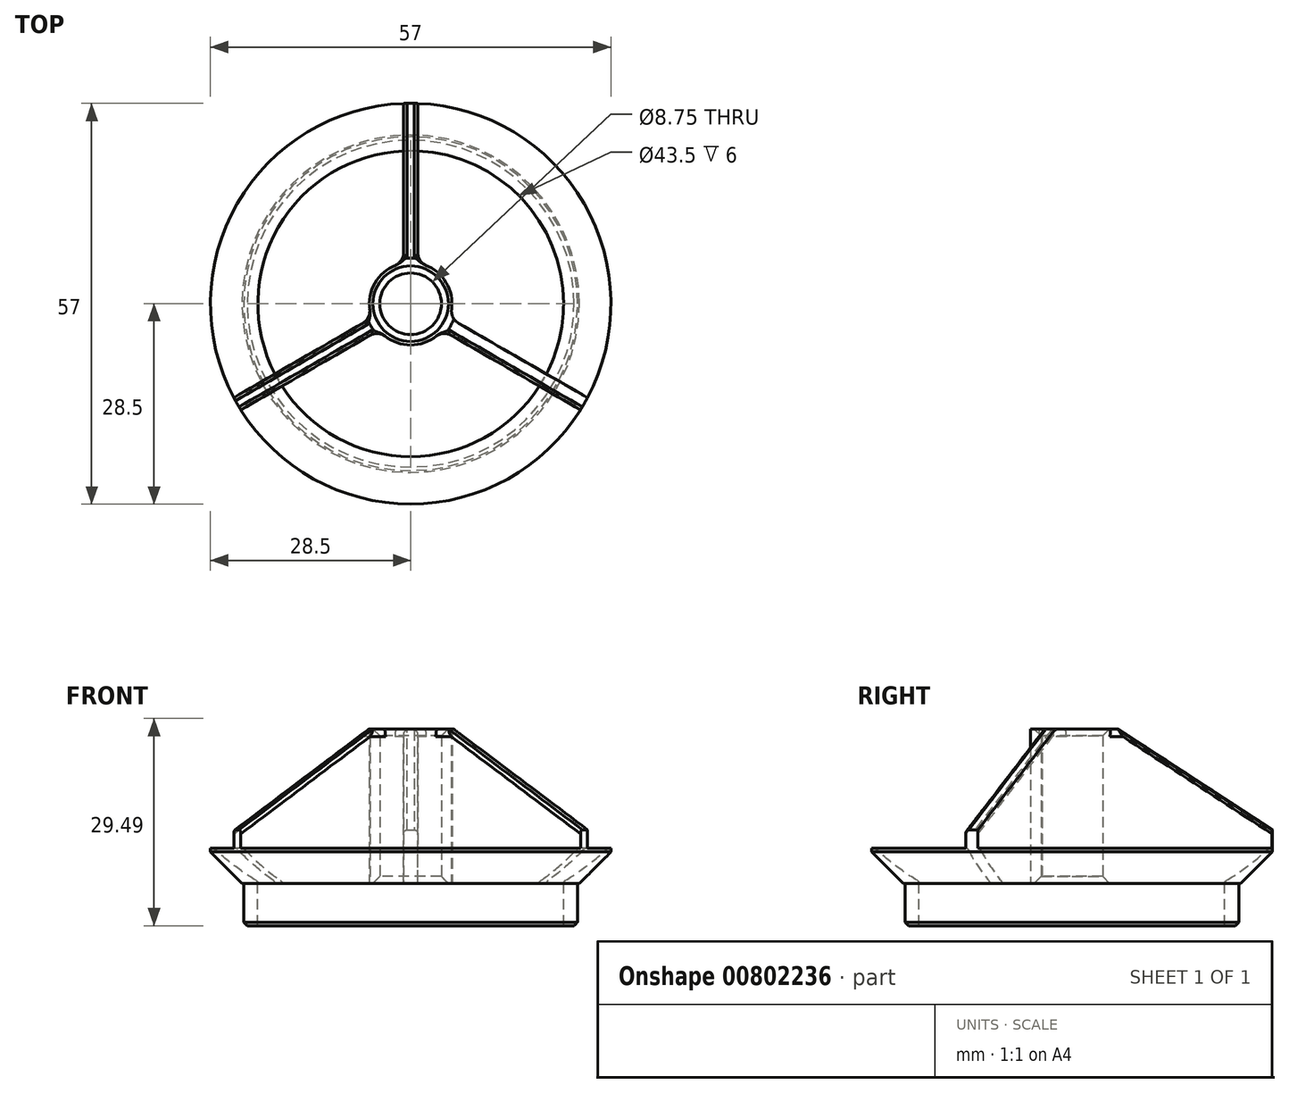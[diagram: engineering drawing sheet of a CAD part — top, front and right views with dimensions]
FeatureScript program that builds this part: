
annotation { "Feature Type Name" : "Feature", "Feature Type Description" : "" }
export const myFeature = defineFeature(function(context is Context, id is Id, definition is map)
    precondition{}
    {
        {
            var Q0;
            Q0=qCreatedBy(makeId("Top.planeOp"),FACE);
            var sketch = newSketch(context, id + "F0", { "sketchPlane" : qUnion([Q0])});
            skCircle(sketch, "E0", {"center": v(0, 0) * mm, "radius": 29.5 * mm});
            skCircle(sketch, "E1", {"center": v(0, 0) * mm, "radius": 4.38 * mm});
            skCircle(sketch, "E2", {"center": v(0, 0) * mm, "radius": 5.88 * mm});
            skCircle(sketch, "E3", {"center": v(0, 0) * mm, "radius": 22.5 * mm});
            skLineSegment(sketch, "E4", {"start": v(-1, 22.48) * mm, "end": v(-1, 5.79) * mm});
            skLineSegment(sketch, "E5", {"start": v(1, 5.79) * mm, "end": v(1, 22.48) * mm});
            skLineSegment(sketch, "E6", {"start": v(-1, 22.48) * mm, "end": v(-1, 29.48) * mm});
            skLineSegment(sketch, "E7", {"start": v(1, 22.48) * mm, "end": v(1, 29.48) * mm});
            skCircle(sketch, "E8", {"center": v(0, 0) * mm, "radius": 28.5 * mm});
            skLineSegment(sketch, "E9.1.0", {"start": v(-19.97, -10.37) * mm, "end": v(-26.03, -13.88) * mm});
            skLineSegment(sketch, "E9.1.1", {"start": v(-18.97, -12.1) * mm, "end": v(-25.03, -15.6) * mm});
            skLineSegment(sketch, "E9.1.2", {"start": v(-18.97, -12.1) * mm, "end": v(-4.51, -3.76) * mm});
            skLineSegment(sketch, "E9.1.3", {"start": v(-5.51, -2.03) * mm, "end": v(-19.97, -10.37) * mm});
            skLineSegment(sketch, "E9.2.0", {"start": v(18.97, -12.1) * mm, "end": v(25.03, -15.6) * mm});
            skLineSegment(sketch, "E9.2.1", {"start": v(19.97, -10.37) * mm, "end": v(26.03, -13.88) * mm});
            skLineSegment(sketch, "E9.2.2", {"start": v(19.97, -10.37) * mm, "end": v(5.51, -2.03) * mm});
            skLineSegment(sketch, "E9.2.3", {"start": v(4.51, -3.76) * mm, "end": v(18.97, -12.1) * mm});
            skSolve(sketch);
        }
        {
            var Q0;
            {var subQ0=sQuery(id+"F0.wireOp",EDGE,"E6");var subQ5=sQuery(id+"F0.wireOp",EDGE,"E8");var subQ6=makeQuery(id+"F0.imprint","INTERSECT",VERTEX,{"derivedFrom":[subQ0,subQ5]});Q0=makeQuery(id+"F0.imprint","IMPRINT",FACE,{"disambiguationData":[TD([[makeQuery(id+"F0.imprint","IMPRINT",EDGE,{"disambiguationData":[TD([[subQ6,-1.0]])],"derivedFrom":subQ5}),1.0]])]});}
            var Q1;
            {var subQ0=sQuery(id+"F0.wireOp",EDGE,"E7");var subQ5=sQuery(id+"F0.wireOp",EDGE,"E8");var subQ7=makeQuery(id+"F0.imprint","INTERSECT",VERTEX,{"derivedFrom":[subQ0,subQ5]});Q1=makeQuery(id+"F0.imprint","IMPRINT",FACE,{"disambiguationData":[TD([[makeQuery(id+"F0.imprint","IMPRINT",EDGE,{"disambiguationData":[TD([[subQ7,1.0]])],"derivedFrom":subQ5}),1.0]])]});}
            var Q2;
            {var subQ0=sQuery(id+"F0.wireOp",EDGE,"6sBZeKKk-kEEp-gHMs-JJ9J-U2pvovovTZg0");var subQ5=sQuery(id+"F0.wireOp",EDGE,"E8");var subQ7=makeQuery(id+"F0.imprint","INTERSECT",VERTEX,{"derivedFrom":[subQ0,subQ5]});Q2=makeQuery(id+"F0.imprint","IMPRINT",FACE,{"disambiguationData":[TD([[makeQuery(id+"F0.imprint","IMPRINT",EDGE,{"disambiguationData":[TD([[subQ7,1.0]])],"derivedFrom":subQ5}),1.0]])]});}
            var Q3;
            {var subQ0=sQuery(id+"F0.wireOp",EDGE,"7a49S09U-4TKs-Mau8-UFGr-jYDSAMmVkobc");var subQ5=sQuery(id+"F0.wireOp",EDGE,"E8");var subQ6=makeQuery(id+"F0.imprint","INTERSECT",VERTEX,{"derivedFrom":[subQ0,subQ5]});Q3=makeQuery(id+"F0.imprint","IMPRINT",FACE,{"disambiguationData":[TD([[makeQuery(id+"F0.imprint","IMPRINT",EDGE,{"disambiguationData":[TD([[subQ6,1.0]])],"derivedFrom":subQ5}),1.0]])]});}
            var Q4;
            {var subQ0=sQuery(id+"F0.wireOp",EDGE,"7a49S09U-4TKs-Mau8-UFGr-jYDSAMmVkobc");var subQ1=sQuery(id+"F0.wireOp",EDGE,"E0");var subQ2=makeQuery(id+"F0.imprint","INTERSECT",VERTEX,{"derivedFrom":[subQ1,subQ0]});Q4=makeQuery(id+"F0.imprint","IMPRINT",FACE,{"disambiguationData":[TD([[makeQuery(id+"F0.imprint","IMPRINT",EDGE,{"disambiguationData":[TD([[subQ2,1.0]])],"derivedFrom":subQ1}),1.0]])]});}
            var Q5;
            {var subQ0=sQuery(id+"F0.wireOp",EDGE,"E6");var subQ1=sQuery(id+"F0.wireOp",EDGE,"E0");var subQ2=makeQuery(id+"F0.imprint","INTERSECT",VERTEX,{"derivedFrom":[subQ1,subQ0]});Q5=makeQuery(id+"F0.imprint","IMPRINT",FACE,{"disambiguationData":[TD([[makeQuery(id+"F0.imprint","IMPRINT",EDGE,{"disambiguationData":[TD([[subQ2,-1.0]])],"derivedFrom":subQ1}),1.0]])]});}
            var Q6;
            {var subQ0=sQuery(id+"F0.wireOp",EDGE,"E7");var subQ1=sQuery(id+"F0.wireOp",EDGE,"E0");var subQ2=makeQuery(id+"F0.imprint","INTERSECT",VERTEX,{"derivedFrom":[subQ1,subQ0]});Q6=makeQuery(id+"F0.imprint","IMPRINT",FACE,{"disambiguationData":[TD([[makeQuery(id+"F0.imprint","IMPRINT",EDGE,{"disambiguationData":[TD([[subQ2,1.0]])],"derivedFrom":subQ1}),1.0]])]});}
            var Q7;
            {var subQ0=sQuery(id+"F0.wireOp",EDGE,"6sBZeKKk-kEEp-gHMs-JJ9J-U2pvovovTZg0");var subQ1=sQuery(id+"F0.wireOp",EDGE,"E0");var subQ2=makeQuery(id+"F0.imprint","INTERSECT",VERTEX,{"derivedFrom":[subQ1,subQ0]});Q7=makeQuery(id+"F0.imprint","IMPRINT",FACE,{"disambiguationData":[TD([[makeQuery(id+"F0.imprint","IMPRINT",EDGE,{"disambiguationData":[TD([[subQ2,1.0]])],"derivedFrom":subQ1}),1.0]])]});}
            var Q8;
            {var subQ0=sQuery(id+"F0.wireOp",EDGE,"kpPb6oPH-wYUV-R5u9-Nvo8-y8tA6iOcowlW");var subQ5=sQuery(id+"F0.wireOp",EDGE,"E8");var subQ7=makeQuery(id+"F0.imprint","INTERSECT",VERTEX,{"derivedFrom":[subQ0,subQ5]});Q8=makeQuery(id+"F0.imprint","IMPRINT",FACE,{"disambiguationData":[TD([[makeQuery(id+"F0.imprint","IMPRINT",EDGE,{"disambiguationData":[TD([[subQ7,1.0]])],"derivedFrom":subQ5}),1.0]])]});}
            var Q9;
            {var subQ0=sQuery(id+"F0.wireOp",EDGE,"kpPb6oPH-wYUV-R5u9-Nvo8-y8tA6iOcowlW");var subQ1=sQuery(id+"F0.wireOp",EDGE,"E0");var subQ2=makeQuery(id+"F0.imprint","INTERSECT",VERTEX,{"derivedFrom":[subQ1,subQ0]});Q9=makeQuery(id+"F0.imprint","IMPRINT",FACE,{"disambiguationData":[TD([[makeQuery(id+"F0.imprint","IMPRINT",EDGE,{"disambiguationData":[TD([[subQ2,1.0]])],"derivedFrom":subQ1}),1.0]])]});}
            var Q10;
            {var subQ0=sQuery(id+"F0.wireOp",EDGE,"64FUqdOZ-ZsVY-jkXw-3n9p-KAZBQBVsTFE5");var subQ1=sQuery(id+"F0.wireOp",EDGE,"E0");var subQ2=makeQuery(id+"F0.imprint","INTERSECT",VERTEX,{"derivedFrom":[subQ1,subQ0]});Q10=makeQuery(id+"F0.imprint","IMPRINT",FACE,{"disambiguationData":[TD([[makeQuery(id+"F0.imprint","IMPRINT",EDGE,{"disambiguationData":[TD([[subQ2,-1.0]])],"derivedFrom":subQ1}),1.0]])]});}
            var Q11;
            {var subQ0=sQuery(id+"F0.wireOp",EDGE,"64FUqdOZ-ZsVY-jkXw-3n9p-KAZBQBVsTFE5");var subQ5=sQuery(id+"F0.wireOp",EDGE,"E8");var subQ6=makeQuery(id+"F0.imprint","INTERSECT",VERTEX,{"derivedFrom":[subQ0,subQ5]});Q11=makeQuery(id+"F0.imprint","IMPRINT",FACE,{"disambiguationData":[TD([[makeQuery(id+"F0.imprint","IMPRINT",EDGE,{"disambiguationData":[TD([[subQ6,-1.0]])],"derivedFrom":subQ5}),1.0]])]});}
            var Q12;
            {var subQ0=sQuery(id+"F0.wireOp",EDGE,"E6");var subQ5=sQuery(id+"F0.wireOp",EDGE,"E8");var subQ6=makeQuery(id+"F0.imprint","INTERSECT",VERTEX,{"derivedFrom":[subQ0,subQ5]});Q12=makeQuery(id+"F0.imprint","IMPRINT",FACE,{"disambiguationData":[TD([[makeQuery(id+"F0.imprint","IMPRINT",EDGE,{"disambiguationData":[TD([[subQ6,1.0]])],"derivedFrom":subQ5}),1.0]])]});}
            var Q13;
            {var subQ0=sQuery(id+"F0.wireOp",EDGE,"E6");var subQ1=sQuery(id+"F0.wireOp",EDGE,"E0");var subQ2=makeQuery(id+"F0.imprint","INTERSECT",VERTEX,{"derivedFrom":[subQ1,subQ0]});Q13=makeQuery(id+"F0.imprint","IMPRINT",FACE,{"disambiguationData":[TD([[makeQuery(id+"F0.imprint","IMPRINT",EDGE,{"disambiguationData":[TD([[subQ2,1.0]])],"derivedFrom":subQ1}),1.0]])]});}
            var Q14;
            {var subQ0=sQuery(id+"F0.wireOp",EDGE,"7a49S09U-4TKs-Mau8-UFGr-jYDSAMmVkobc");var subQ5=sQuery(id+"F0.wireOp",EDGE,"E8");var subQ6=makeQuery(id+"F0.imprint","INTERSECT",VERTEX,{"derivedFrom":[subQ0,subQ5]});Q14=makeQuery(id+"F0.imprint","IMPRINT",FACE,{"disambiguationData":[TD([[makeQuery(id+"F0.imprint","IMPRINT",EDGE,{"disambiguationData":[TD([[subQ6,-1.0]])],"derivedFrom":subQ5}),1.0]])]});}
            var Q15;
            {var subQ0=sQuery(id+"F0.wireOp",EDGE,"7a49S09U-4TKs-Mau8-UFGr-jYDSAMmVkobc");var subQ1=sQuery(id+"F0.wireOp",EDGE,"E0");var subQ2=makeQuery(id+"F0.imprint","INTERSECT",VERTEX,{"derivedFrom":[subQ1,subQ0]});Q15=makeQuery(id+"F0.imprint","IMPRINT",FACE,{"disambiguationData":[TD([[makeQuery(id+"F0.imprint","IMPRINT",EDGE,{"disambiguationData":[TD([[subQ2,-1.0]])],"derivedFrom":subQ1}),1.0]])]});}
            extrude(context, id + "F1", {"entities" : qUnion([Q0, Q1, Q2, Q3, Q4, Q5, Q6, Q7, Q8, Q9, Q10, Q11, Q12, Q13, Q14, Q15]), "depth" : 5 * mm, "offsetDistance" : 25 * mm});
        }
        {
            var Q0;
            {var subQ0=sQuery(id+"F0.wireOp",EDGE,"E9.2.2");Q0=makeQuery(id+"F0.imprint","IMPRINT",FACE,{"disambiguationData":[TD([[makeQuery(id+"F0.imprint","IMPRINT",EDGE,{"derivedFrom":subQ0}),1.0]])]});}
            var Q1;
            Q1=makeQuery(id+"F0.imprint","IMPRINT",FACE,{"disambiguationData":[TD([[makeQuery(id+"F0.imprint","IMPRINT",EDGE,{"derivedFrom":sQuery(id+"F0.wireOp",EDGE,"E1")}),-1.0]])]});
            var Q2;
            {var subQ0=sQuery(id+"F0.wireOp",EDGE,"E9.1.2");Q2=makeQuery(id+"F0.imprint","IMPRINT",FACE,{"disambiguationData":[TD([[makeQuery(id+"F0.imprint","IMPRINT",EDGE,{"derivedFrom":subQ0}),1.0]])]});}
            var Q3;
            {var subQ0=sQuery(id+"F0.wireOp",EDGE,"E4");Q3=makeQuery(id+"F0.imprint","IMPRINT",FACE,{"disambiguationData":[TD([[makeQuery(id+"F0.imprint","IMPRINT",EDGE,{"derivedFrom":subQ0}),1.0]])]});}
            var Q4;
            {var subQ0=sQuery(id+"F0.wireOp",EDGE,"E9.1.0");var subQ5=sQuery(id+"F0.wireOp",EDGE,"E8");var subQ6=makeQuery(id+"F0.imprint","INTERSECT",VERTEX,{"derivedFrom":[subQ5,subQ0]});Q4=makeQuery(id+"F0.imprint","IMPRINT",FACE,{"disambiguationData":[TD([[makeQuery(id+"F0.imprint","IMPRINT",EDGE,{"disambiguationData":[TD([[subQ6,-1.0]])],"derivedFrom":subQ5}),1.0]])]});}
            var Q5;
            {var subQ0=sQuery(id+"F0.wireOp",EDGE,"E9.2.0");var subQ5=sQuery(id+"F0.wireOp",EDGE,"E8");var subQ6=makeQuery(id+"F0.imprint","INTERSECT",VERTEX,{"derivedFrom":[subQ5,subQ0]});Q5=makeQuery(id+"F0.imprint","IMPRINT",FACE,{"disambiguationData":[TD([[makeQuery(id+"F0.imprint","IMPRINT",EDGE,{"disambiguationData":[TD([[subQ6,-1.0]])],"derivedFrom":subQ5}),1.0]])]});}
            var Q6;
            {var subQ0=sQuery(id+"F0.wireOp",EDGE,"E6");var subQ5=sQuery(id+"F0.wireOp",EDGE,"E8");var subQ7=makeQuery(id+"F0.imprint","INTERSECT",VERTEX,{"derivedFrom":[subQ0,subQ5]});Q6=makeQuery(id+"F0.imprint","IMPRINT",FACE,{"disambiguationData":[TD([[makeQuery(id+"F0.imprint","IMPRINT",EDGE,{"disambiguationData":[TD([[subQ7,1.0]])],"derivedFrom":subQ5}),1.0]])]});}
            var Q7;
            {var subQ0=sQuery(id+"F0.wireOp",EDGE,"E9.2.0");var subQ1=sQuery(id+"F0.wireOp",EDGE,"E0");var subQ2=makeQuery(id+"F0.imprint","INTERSECT",VERTEX,{"derivedFrom":[subQ1,subQ0]});Q7=makeQuery(id+"F0.imprint","IMPRINT",FACE,{"disambiguationData":[TD([[makeQuery(id+"F0.imprint","IMPRINT",EDGE,{"disambiguationData":[TD([[subQ2,-1.0]])],"derivedFrom":subQ1}),1.0]])]});}
            var Q8;
            {var subQ0=sQuery(id+"F0.wireOp",EDGE,"E9.1.0");var subQ1=sQuery(id+"F0.wireOp",EDGE,"E0");var subQ2=makeQuery(id+"F0.imprint","INTERSECT",VERTEX,{"derivedFrom":[subQ1,subQ0]});Q8=makeQuery(id+"F0.imprint","IMPRINT",FACE,{"disambiguationData":[TD([[makeQuery(id+"F0.imprint","IMPRINT",EDGE,{"disambiguationData":[TD([[subQ2,-1.0]])],"derivedFrom":subQ1}),1.0]])]});}
            var Q9;
            {var subQ0=sQuery(id+"F0.wireOp",EDGE,"E6");var subQ1=sQuery(id+"F0.wireOp",EDGE,"E0");var subQ2=makeQuery(id+"F0.imprint","INTERSECT",VERTEX,{"derivedFrom":[subQ1,subQ0]});Q9=makeQuery(id+"F0.imprint","IMPRINT",FACE,{"disambiguationData":[TD([[makeQuery(id+"F0.imprint","IMPRINT",EDGE,{"disambiguationData":[TD([[subQ2,1.0]])],"derivedFrom":subQ1}),1.0]])]});}
            extrude(context, id + "F2", {"entities" : qUnion([Q0, Q1, Q2, Q3, Q4, Q5, Q6, Q7, Q8, Q9]), "operationType" : NewBodyOperationType.ADD, "depth" : 22 * mm, "offsetDistance" : 25 * mm});
        }
        {
            var Q0;
            Q0=makeQuery(id+"F1.opExtrude","CAP_EDGE",EDGE,{"disambiguationData":[OSD([sQuery(id+"F0.wireOp",EDGE,"E0")])],"isStart":true});
            var Q1;
            Q1=makeQuery(id+"F1.opExtrude","CAP_EDGE",EDGE,{"disambiguationData":[OSD([sQuery(id+"F0.wireOp",EDGE,"E3")])],"isStart":false});
            chamfer(context, id + "F3", {"entities" : qUnion([Q0, Q1]), "width" : 5.5 * mm, "tangentPropagation" : true});
        }
        {
            var Q0;
            Q0=qCreatedBy(makeId("Top.planeOp"),FACE);
            var sketch = newSketch(context, id + "F4", { "sketchPlane" : qUnion([Q0]), "disableImprinting" : false});
            skCircle(sketch, "E10", {"center": v(0, 0) * mm, "radius": 23.75 * mm});
            skCircle(sketch, "E11", {"center": v(0, 0) * mm, "radius": 21.75 * mm});
            skLineSegment(sketch, "E12", {"start": v(0, -21.75) * mm, "end": v(0, -23.75) * mm});
            skLineSegment(sketch, "E13.1.0", {"start": v(18.84, -10.88) * mm, "end": v(20.57, -11.88) * mm});
            skLineSegment(sketch, "E13.2.0", {"start": v(18.84, 10.87) * mm, "end": v(20.57, 11.87) * mm});
            skLineSegment(sketch, "E14.2.3.0", {"start": v(0, 21.75) * mm, "end": v(0, 23.75) * mm});
            skLineSegment(sketch, "E14.2.4.0", {"start": v(-18.84, 10.88) * mm, "end": v(-20.57, 11.88) * mm});
            skLineSegment(sketch, "E14.2.5.0", {"start": v(-18.84, -10.88) * mm, "end": v(-20.57, -11.88) * mm});
            skSolve(sketch);
        }
        {
            var Q0;
            Q0=makeQuery(id+"F4.imprint","IMPRINT",FACE,{"disambiguationData":[TD([[makeQuery(id+"F4.imprint","IMPRINT",EDGE,{"derivedFrom":sQuery(id+"F4.wireOp",EDGE,"E10")}),1.0]])]});
            extrude(context, id + "F5", {"entities" : qUnion([Q0]), "operationType" : NewBodyOperationType.ADD, "oppositeDirection" : true, "depth" : 6 * mm, "offsetDistance" : 25 * mm, "hasSecondDirection" : true, "secondDirectionOppositeDirection" : false, "secondDirectionDepth" : 0.5 * mm});
        }
        {
            var Q0;
            {var subQ0=sQuery(id+"F0.wireOp",EDGE,"E0");Q0=makeQuery(id+"F2.opExtrude","CAP_EDGE",EDGE,{"disambiguationData":[OSD([subQ0]),TDD([makeQuery(id+"F0.imprint","IMPRINT",EDGE,{"disambiguationData":[TD([[makeQuery(id+"F0.imprint","INTERSECT",VERTEX,{"derivedFrom":[subQ0,sQuery(id+"F0.wireOp",EDGE,"64FUqdOZ-ZsVY-jkXw-3n9p-KAZBQBVsTFE5")]}),-1.0]])],"derivedFrom":subQ0})])],"isStart":false});}
            var Q1;
            {var subQ0=sQuery(id+"F0.wireOp",EDGE,"E0");Q1=makeQuery(id+"F2.opExtrude","CAP_EDGE",EDGE,{"disambiguationData":[OSD([subQ0]),TDD([makeQuery(id+"F0.imprint","IMPRINT",EDGE,{"disambiguationData":[TD([[makeQuery(id+"F0.imprint","INTERSECT",VERTEX,{"derivedFrom":[subQ0,sQuery(id+"F0.wireOp",EDGE,"E6")]}),1.0]])],"derivedFrom":subQ0})])],"isStart":false});}
            var Q2;
            {var subQ0=sQuery(id+"F0.wireOp",EDGE,"E0");Q2=makeQuery(id+"F2.opExtrude","CAP_EDGE",EDGE,{"disambiguationData":[OSD([subQ0]),TDD([makeQuery(id+"F0.imprint","IMPRINT",EDGE,{"disambiguationData":[TD([[makeQuery(id+"F0.imprint","INTERSECT",VERTEX,{"derivedFrom":[subQ0,sQuery(id+"F0.wireOp",EDGE,"7a49S09U-4TKs-Mau8-UFGr-jYDSAMmVkobc")]}),-1.0]])],"derivedFrom":subQ0})])],"isStart":false});}
            var Q3;
            {var subQ0=sQuery(id+"F0.wireOp",EDGE,"E0");Q3=makeQuery(id+"F2.opExtrude","CAP_EDGE",EDGE,{"disambiguationData":[OSD([subQ0]),TDD([makeQuery(id+"F0.imprint","IMPRINT",EDGE,{"disambiguationData":[TD([[makeQuery(id+"F0.imprint","INTERSECT",VERTEX,{"derivedFrom":[subQ0,sQuery(id+"F0.wireOp",EDGE,"kpPb6oPH-wYUV-R5u9-Nvo8-y8tA6iOcowlW")]}),1.0]])],"derivedFrom":subQ0})])],"isStart":false});}
            chamfer(context, id + "F6", {"entities" : qUnion([Q0, Q1, Q2, Q3]), "chamferType" : ChamferType.TWO_OFFSETS, "width1" : 23 * mm, "oppositeDirection" : false, "width2" : 15 * mm, "tangentPropagation" : true});
        }
        {
            var Q0;
            Q0=makeQuery(id+"F2.opExtrude","CAP_EDGE",EDGE,{"disambiguationData":[OSD([sQuery(id+"F0.wireOp",EDGE,"E1")])],"isStart":true});
            var Q1;
            Q1=makeQuery(id+"F2.opExtrude","CAP_EDGE",EDGE,{"disambiguationData":[OSD([sQuery(id+"F0.wireOp",EDGE,"E1")])],"isStart":false});
            chamfer(context, id + "F7", {"entities" : qUnion([Q0, Q1]), "width" : 1 * mm, "tangentPropagation" : true});
        }
        {
            var Q0;
            {var subQ0=sQuery(id+"F0.wireOp",EDGE,"E6");var subQ1=sQuery(id+"F0.wireOp",EDGE,"E0");Q0=makeQuery(id+"F6.opChamfer","BLEND_EDGE",EDGE,{"blendedFrom":[makeQuery(id+"F2.opExtrude","CAP_EDGE",EDGE,{"disambiguationData":[OSD([subQ1]),TDD([makeQuery(id+"F0.imprint","IMPRINT",EDGE,{"disambiguationData":[TD([[makeQuery(id+"F0.imprint","INTERSECT",VERTEX,{"derivedFrom":[subQ1,subQ0]}),1.0]])],"derivedFrom":subQ1})])],"isStart":false}),makeQuery(id+"F2.opExtrude","SWEPT_FACE",FACE,{"disambiguationData":[OSD([sQuery(id+"F0.wireOp",EDGE,"E4"),subQ0])]})],"blendedInto":[makeQuery(id+"F2.opExtrude","SWEPT_FACE",FACE,{"disambiguationData":[OSD([sQuery(id+"F0.wireOp",EDGE,"E4"),subQ0])]})]});}
            var Q1;
            {var subQ0=sQuery(id+"F0.wireOp",EDGE,"E7");var subQ1=sQuery(id+"F0.wireOp",EDGE,"E0");Q1=makeQuery(id+"F6.opChamfer","BLEND_EDGE",EDGE,{"blendedFrom":[makeQuery(id+"F2.opExtrude","CAP_EDGE",EDGE,{"disambiguationData":[OSD([subQ1]),TDD([makeQuery(id+"F0.imprint","IMPRINT",EDGE,{"disambiguationData":[TD([[makeQuery(id+"F0.imprint","INTERSECT",VERTEX,{"derivedFrom":[subQ1,sQuery(id+"F0.wireOp",EDGE,"E6")]}),1.0]])],"derivedFrom":subQ1})])],"isStart":false}),makeQuery(id+"F2.opExtrude","SWEPT_FACE",FACE,{"disambiguationData":[OSD([sQuery(id+"F0.wireOp",EDGE,"E5"),subQ0])]})],"blendedInto":[makeQuery(id+"F2.opExtrude","SWEPT_FACE",FACE,{"disambiguationData":[OSD([sQuery(id+"F0.wireOp",EDGE,"E5"),subQ0])]})]});}
            var Q2;
            {var subQ0=sQuery(id+"F0.wireOp",EDGE,"E9.1.0");var subQ1=sQuery(id+"F0.wireOp",EDGE,"E0");Q2=makeQuery(id+"F6.opChamfer","BLEND_EDGE",EDGE,{"blendedFrom":[makeQuery(id+"F2.opExtrude","CAP_EDGE",EDGE,{"disambiguationData":[OSD([subQ1]),TDD([makeQuery(id+"F0.imprint","IMPRINT",EDGE,{"disambiguationData":[TD([[makeQuery(id+"F0.imprint","INTERSECT",VERTEX,{"derivedFrom":[subQ1,subQ0]}),-1.0]])],"derivedFrom":subQ1})])],"isStart":false}),makeQuery(id+"F2.opExtrude","SWEPT_FACE",FACE,{"disambiguationData":[OSD([subQ0,sQuery(id+"F0.wireOp",EDGE,"E9.1.3")])]})],"blendedInto":[makeQuery(id+"F2.opExtrude","SWEPT_FACE",FACE,{"disambiguationData":[OSD([subQ0,sQuery(id+"F0.wireOp",EDGE,"E9.1.3")])]})]});}
            var Q3;
            {var subQ0=sQuery(id+"F0.wireOp",EDGE,"E9.1.1");var subQ1=sQuery(id+"F0.wireOp",EDGE,"E0");Q3=makeQuery(id+"F6.opChamfer","BLEND_EDGE",EDGE,{"blendedFrom":[makeQuery(id+"F2.opExtrude","CAP_EDGE",EDGE,{"disambiguationData":[OSD([subQ1]),TDD([makeQuery(id+"F0.imprint","IMPRINT",EDGE,{"disambiguationData":[TD([[makeQuery(id+"F0.imprint","INTERSECT",VERTEX,{"derivedFrom":[subQ1,sQuery(id+"F0.wireOp",EDGE,"E9.1.0")]}),-1.0]])],"derivedFrom":subQ1})])],"isStart":false}),makeQuery(id+"F2.opExtrude","SWEPT_FACE",FACE,{"disambiguationData":[OSD([subQ0,sQuery(id+"F0.wireOp",EDGE,"E9.1.2")])]})],"blendedInto":[makeQuery(id+"F2.opExtrude","SWEPT_FACE",FACE,{"disambiguationData":[OSD([subQ0,sQuery(id+"F0.wireOp",EDGE,"E9.1.2")])]})]});}
            var Q4;
            {var subQ0=sQuery(id+"F0.wireOp",EDGE,"E9.2.0");var subQ1=sQuery(id+"F0.wireOp",EDGE,"E0");Q4=makeQuery(id+"F6.opChamfer","BLEND_EDGE",EDGE,{"blendedFrom":[makeQuery(id+"F2.opExtrude","CAP_EDGE",EDGE,{"disambiguationData":[OSD([subQ1]),TDD([makeQuery(id+"F0.imprint","IMPRINT",EDGE,{"disambiguationData":[TD([[makeQuery(id+"F0.imprint","INTERSECT",VERTEX,{"derivedFrom":[subQ1,subQ0]}),-1.0]])],"derivedFrom":subQ1})])],"isStart":false}),makeQuery(id+"F2.opExtrude","SWEPT_FACE",FACE,{"disambiguationData":[OSD([subQ0,sQuery(id+"F0.wireOp",EDGE,"E9.2.3")])]})],"blendedInto":[makeQuery(id+"F2.opExtrude","SWEPT_FACE",FACE,{"disambiguationData":[OSD([subQ0,sQuery(id+"F0.wireOp",EDGE,"E9.2.3")])]})]});}
            var Q5;
            {var subQ0=sQuery(id+"F0.wireOp",EDGE,"E0");var subQ1=makeQuery(id+"F0.imprint","IMPRINT",EDGE,{"disambiguationData":[TD([[makeQuery(id+"F0.imprint","INTERSECT",VERTEX,{"derivedFrom":[subQ0,sQuery(id+"F0.wireOp",EDGE,"E6")]}),1.0]])],"derivedFrom":subQ0});Q5=makeQuery(id+"F6.opChamfer","BLEND_EDGE",EDGE,{"blendedFrom":[makeQuery(id+"F2.opExtrude","CAP_EDGE",EDGE,{"disambiguationData":[OSD([subQ0]),TDD([subQ1])],"isStart":false}),makeQuery(id+"F3.opChamfer","SPLIT",FACE,{"disambiguationData":[OD(0.0)],"derivedFrom":makeQuery(id+"F2.boolean.opBoolean","MERGE",FACE,{"derivedFrom":[makeQuery(id+"F1.opExtrude","SWEPT_FACE",FACE,{"disambiguationData":[OSD([subQ0])]}),makeQuery(id+"F2.opExtrude","SWEPT_FACE",FACE,{"disambiguationData":[OSD([subQ0]),TDD([subQ1])]}),makeQuery(id+"F2.opExtrude","SWEPT_FACE",FACE,{"disambiguationData":[OSD([subQ0]),TDD([makeQuery(id+"F0.imprint","IMPRINT",EDGE,{"disambiguationData":[TD([[makeQuery(id+"F0.imprint","INTERSECT",VERTEX,{"derivedFrom":[subQ0,sQuery(id+"F0.wireOp",EDGE,"E9.1.0")]}),-1.0]])],"derivedFrom":subQ0})])]}),makeQuery(id+"F2.opExtrude","SWEPT_FACE",FACE,{"disambiguationData":[OSD([subQ0]),TDD([makeQuery(id+"F0.imprint","IMPRINT",EDGE,{"disambiguationData":[TD([[makeQuery(id+"F0.imprint","INTERSECT",VERTEX,{"derivedFrom":[subQ0,sQuery(id+"F0.wireOp",EDGE,"E9.2.0")]}),-1.0]])],"derivedFrom":subQ0})])]})]})})],"blendedInto":[makeQuery(id+"F3.opChamfer","SPLIT",FACE,{"disambiguationData":[OD(0.0)],"derivedFrom":makeQuery(id+"F2.boolean.opBoolean","MERGE",FACE,{"derivedFrom":[makeQuery(id+"F1.opExtrude","SWEPT_FACE",FACE,{"disambiguationData":[OSD([subQ0])]}),makeQuery(id+"F2.opExtrude","SWEPT_FACE",FACE,{"disambiguationData":[OSD([subQ0]),TDD([subQ1])]}),makeQuery(id+"F2.opExtrude","SWEPT_FACE",FACE,{"disambiguationData":[OSD([subQ0]),TDD([makeQuery(id+"F0.imprint","IMPRINT",EDGE,{"disambiguationData":[TD([[makeQuery(id+"F0.imprint","INTERSECT",VERTEX,{"derivedFrom":[subQ0,sQuery(id+"F0.wireOp",EDGE,"E9.1.0")]}),-1.0]])],"derivedFrom":subQ0})])]}),makeQuery(id+"F2.opExtrude","SWEPT_FACE",FACE,{"disambiguationData":[OSD([subQ0]),TDD([makeQuery(id+"F0.imprint","IMPRINT",EDGE,{"disambiguationData":[TD([[makeQuery(id+"F0.imprint","INTERSECT",VERTEX,{"derivedFrom":[subQ0,sQuery(id+"F0.wireOp",EDGE,"E9.2.0")]}),-1.0]])],"derivedFrom":subQ0})])]})]})})]});}
            var Q6;
            {var subQ0=sQuery(id+"F0.wireOp",EDGE,"E0");var subQ1=sQuery(id+"F0.wireOp",EDGE,"E7");Q6=makeQuery(id+"F9.opFillet","BLEND_EDGE",EDGE,{"blendedFrom":[makeQuery(id+"F2.boolean.opBoolean","INTERSECT",EDGE,{"derivedFrom":[makeQuery(id+"F1.opExtrude","CAP_FACE",FACE,{"disambiguationData":[OSD([subQ0,sQuery(id+"F0.wireOp",EDGE,"E3")])],"isStart":false}),makeQuery(id+"F2.opExtrude","SWEPT_FACE",FACE,{"disambiguationData":[OSD([sQuery(id+"F0.wireOp",EDGE,"E5"),subQ1])]})]}),makeQuery(id+"F3.opChamfer","SPLIT",FACE,{"disambiguationData":[OD(0.0)],"derivedFrom":makeQuery(id+"F2.boolean.opBoolean","MERGE",FACE,{"derivedFrom":[makeQuery(id+"F1.opExtrude","SWEPT_FACE",FACE,{"disambiguationData":[OSD([subQ0])]}),makeQuery(id+"F2.opExtrude","SWEPT_FACE",FACE,{"disambiguationData":[OSD([subQ0]),TDD([makeQuery(id+"F0.imprint","IMPRINT",EDGE,{"disambiguationData":[TD([[makeQuery(id+"F0.imprint","INTERSECT",VERTEX,{"derivedFrom":[subQ0,sQuery(id+"F0.wireOp",EDGE,"E6")]}),1.0]])],"derivedFrom":subQ0})])]}),makeQuery(id+"F2.opExtrude","SWEPT_FACE",FACE,{"disambiguationData":[OSD([subQ0]),TDD([makeQuery(id+"F0.imprint","IMPRINT",EDGE,{"disambiguationData":[TD([[makeQuery(id+"F0.imprint","INTERSECT",VERTEX,{"derivedFrom":[subQ0,sQuery(id+"F0.wireOp",EDGE,"E9.1.0")]}),-1.0]])],"derivedFrom":subQ0})])]}),makeQuery(id+"F2.opExtrude","SWEPT_FACE",FACE,{"disambiguationData":[OSD([subQ0]),TDD([makeQuery(id+"F0.imprint","IMPRINT",EDGE,{"disambiguationData":[TD([[makeQuery(id+"F0.imprint","INTERSECT",VERTEX,{"derivedFrom":[subQ0,sQuery(id+"F0.wireOp",EDGE,"E9.2.0")]}),-1.0]])],"derivedFrom":subQ0})])]})]})})],"blendedInto":[makeQuery(id+"F3.opChamfer","SPLIT",FACE,{"disambiguationData":[OD(0.0)],"derivedFrom":makeQuery(id+"F2.boolean.opBoolean","MERGE",FACE,{"derivedFrom":[makeQuery(id+"F1.opExtrude","SWEPT_FACE",FACE,{"disambiguationData":[OSD([subQ0])]}),makeQuery(id+"F2.opExtrude","SWEPT_FACE",FACE,{"disambiguationData":[OSD([subQ0]),TDD([makeQuery(id+"F0.imprint","IMPRINT",EDGE,{"disambiguationData":[TD([[makeQuery(id+"F0.imprint","INTERSECT",VERTEX,{"derivedFrom":[subQ0,sQuery(id+"F0.wireOp",EDGE,"E6")]}),1.0]])],"derivedFrom":subQ0})])]}),makeQuery(id+"F2.opExtrude","SWEPT_FACE",FACE,{"disambiguationData":[OSD([subQ0]),TDD([makeQuery(id+"F0.imprint","IMPRINT",EDGE,{"disambiguationData":[TD([[makeQuery(id+"F0.imprint","INTERSECT",VERTEX,{"derivedFrom":[subQ0,sQuery(id+"F0.wireOp",EDGE,"E9.1.0")]}),-1.0]])],"derivedFrom":subQ0})])]}),makeQuery(id+"F2.opExtrude","SWEPT_FACE",FACE,{"disambiguationData":[OSD([subQ0]),TDD([makeQuery(id+"F0.imprint","IMPRINT",EDGE,{"disambiguationData":[TD([[makeQuery(id+"F0.imprint","INTERSECT",VERTEX,{"derivedFrom":[subQ0,sQuery(id+"F0.wireOp",EDGE,"E9.2.0")]}),-1.0]])],"derivedFrom":subQ0})])]})]})})]});}
            var Q7;
            {var subQ0=sQuery(id+"F0.wireOp",EDGE,"E0");var subQ1=sQuery(id+"F0.wireOp",EDGE,"E6");Q7=makeQuery(id+"F9.opFillet","BLEND_EDGE",EDGE,{"blendedFrom":[makeQuery(id+"F2.boolean.opBoolean","INTERSECT",EDGE,{"derivedFrom":[makeQuery(id+"F1.opExtrude","CAP_FACE",FACE,{"disambiguationData":[OSD([subQ0,sQuery(id+"F0.wireOp",EDGE,"E3")])],"isStart":false}),makeQuery(id+"F2.opExtrude","SWEPT_FACE",FACE,{"disambiguationData":[OSD([sQuery(id+"F0.wireOp",EDGE,"E4"),subQ1])]})]}),makeQuery(id+"F3.opChamfer","SPLIT",FACE,{"disambiguationData":[OD(0.0)],"derivedFrom":makeQuery(id+"F2.boolean.opBoolean","MERGE",FACE,{"derivedFrom":[makeQuery(id+"F1.opExtrude","SWEPT_FACE",FACE,{"disambiguationData":[OSD([subQ0])]}),makeQuery(id+"F2.opExtrude","SWEPT_FACE",FACE,{"disambiguationData":[OSD([subQ0]),TDD([makeQuery(id+"F0.imprint","IMPRINT",EDGE,{"disambiguationData":[TD([[makeQuery(id+"F0.imprint","INTERSECT",VERTEX,{"derivedFrom":[subQ0,subQ1]}),1.0]])],"derivedFrom":subQ0})])]}),makeQuery(id+"F2.opExtrude","SWEPT_FACE",FACE,{"disambiguationData":[OSD([subQ0]),TDD([makeQuery(id+"F0.imprint","IMPRINT",EDGE,{"disambiguationData":[TD([[makeQuery(id+"F0.imprint","INTERSECT",VERTEX,{"derivedFrom":[subQ0,sQuery(id+"F0.wireOp",EDGE,"E9.1.0")]}),-1.0]])],"derivedFrom":subQ0})])]}),makeQuery(id+"F2.opExtrude","SWEPT_FACE",FACE,{"disambiguationData":[OSD([subQ0]),TDD([makeQuery(id+"F0.imprint","IMPRINT",EDGE,{"disambiguationData":[TD([[makeQuery(id+"F0.imprint","INTERSECT",VERTEX,{"derivedFrom":[subQ0,sQuery(id+"F0.wireOp",EDGE,"E9.2.0")]}),-1.0]])],"derivedFrom":subQ0})])]})]})})],"blendedInto":[makeQuery(id+"F3.opChamfer","SPLIT",FACE,{"disambiguationData":[OD(0.0)],"derivedFrom":makeQuery(id+"F2.boolean.opBoolean","MERGE",FACE,{"derivedFrom":[makeQuery(id+"F1.opExtrude","SWEPT_FACE",FACE,{"disambiguationData":[OSD([subQ0])]}),makeQuery(id+"F2.opExtrude","SWEPT_FACE",FACE,{"disambiguationData":[OSD([subQ0]),TDD([makeQuery(id+"F0.imprint","IMPRINT",EDGE,{"disambiguationData":[TD([[makeQuery(id+"F0.imprint","INTERSECT",VERTEX,{"derivedFrom":[subQ0,subQ1]}),1.0]])],"derivedFrom":subQ0})])]}),makeQuery(id+"F2.opExtrude","SWEPT_FACE",FACE,{"disambiguationData":[OSD([subQ0]),TDD([makeQuery(id+"F0.imprint","IMPRINT",EDGE,{"disambiguationData":[TD([[makeQuery(id+"F0.imprint","INTERSECT",VERTEX,{"derivedFrom":[subQ0,sQuery(id+"F0.wireOp",EDGE,"E9.1.0")]}),-1.0]])],"derivedFrom":subQ0})])]}),makeQuery(id+"F2.opExtrude","SWEPT_FACE",FACE,{"disambiguationData":[OSD([subQ0]),TDD([makeQuery(id+"F0.imprint","IMPRINT",EDGE,{"disambiguationData":[TD([[makeQuery(id+"F0.imprint","INTERSECT",VERTEX,{"derivedFrom":[subQ0,sQuery(id+"F0.wireOp",EDGE,"E9.2.0")]}),-1.0]])],"derivedFrom":subQ0})])]})]})})]});}
            var Q8;
            {var subQ0=sQuery(id+"F0.wireOp",EDGE,"E0");var subQ1=makeQuery(id+"F0.imprint","IMPRINT",EDGE,{"disambiguationData":[TD([[makeQuery(id+"F0.imprint","INTERSECT",VERTEX,{"derivedFrom":[subQ0,sQuery(id+"F0.wireOp",EDGE,"E9.1.0")]}),-1.0]])],"derivedFrom":subQ0});Q8=makeQuery(id+"F6.opChamfer","BLEND_EDGE",EDGE,{"blendedFrom":[makeQuery(id+"F2.opExtrude","CAP_EDGE",EDGE,{"disambiguationData":[OSD([subQ0]),TDD([subQ1])],"isStart":false}),makeQuery(id+"F3.opChamfer","SPLIT",FACE,{"disambiguationData":[OD(1.0)],"derivedFrom":makeQuery(id+"F2.boolean.opBoolean","MERGE",FACE,{"derivedFrom":[makeQuery(id+"F1.opExtrude","SWEPT_FACE",FACE,{"disambiguationData":[OSD([subQ0])]}),makeQuery(id+"F2.opExtrude","SWEPT_FACE",FACE,{"disambiguationData":[OSD([subQ0]),TDD([makeQuery(id+"F0.imprint","IMPRINT",EDGE,{"disambiguationData":[TD([[makeQuery(id+"F0.imprint","INTERSECT",VERTEX,{"derivedFrom":[subQ0,sQuery(id+"F0.wireOp",EDGE,"E6")]}),1.0]])],"derivedFrom":subQ0})])]}),makeQuery(id+"F2.opExtrude","SWEPT_FACE",FACE,{"disambiguationData":[OSD([subQ0]),TDD([subQ1])]}),makeQuery(id+"F2.opExtrude","SWEPT_FACE",FACE,{"disambiguationData":[OSD([subQ0]),TDD([makeQuery(id+"F0.imprint","IMPRINT",EDGE,{"disambiguationData":[TD([[makeQuery(id+"F0.imprint","INTERSECT",VERTEX,{"derivedFrom":[subQ0,sQuery(id+"F0.wireOp",EDGE,"E9.2.0")]}),-1.0]])],"derivedFrom":subQ0})])]})]})})],"blendedInto":[makeQuery(id+"F3.opChamfer","SPLIT",FACE,{"disambiguationData":[OD(1.0)],"derivedFrom":makeQuery(id+"F2.boolean.opBoolean","MERGE",FACE,{"derivedFrom":[makeQuery(id+"F1.opExtrude","SWEPT_FACE",FACE,{"disambiguationData":[OSD([subQ0])]}),makeQuery(id+"F2.opExtrude","SWEPT_FACE",FACE,{"disambiguationData":[OSD([subQ0]),TDD([makeQuery(id+"F0.imprint","IMPRINT",EDGE,{"disambiguationData":[TD([[makeQuery(id+"F0.imprint","INTERSECT",VERTEX,{"derivedFrom":[subQ0,sQuery(id+"F0.wireOp",EDGE,"E6")]}),1.0]])],"derivedFrom":subQ0})])]}),makeQuery(id+"F2.opExtrude","SWEPT_FACE",FACE,{"disambiguationData":[OSD([subQ0]),TDD([subQ1])]}),makeQuery(id+"F2.opExtrude","SWEPT_FACE",FACE,{"disambiguationData":[OSD([subQ0]),TDD([makeQuery(id+"F0.imprint","IMPRINT",EDGE,{"disambiguationData":[TD([[makeQuery(id+"F0.imprint","INTERSECT",VERTEX,{"derivedFrom":[subQ0,sQuery(id+"F0.wireOp",EDGE,"E9.2.0")]}),-1.0]])],"derivedFrom":subQ0})])]})]})})]});}
            var Q9;
            {var subQ0=sQuery(id+"F0.wireOp",EDGE,"E0");var subQ1=sQuery(id+"F0.wireOp",EDGE,"E9.1.0");Q9=makeQuery(id+"F9.opFillet","BLEND_EDGE",EDGE,{"blendedFrom":[makeQuery(id+"F2.boolean.opBoolean","INTERSECT",EDGE,{"derivedFrom":[makeQuery(id+"F1.opExtrude","CAP_FACE",FACE,{"disambiguationData":[OSD([subQ0,sQuery(id+"F0.wireOp",EDGE,"E3")])],"isStart":false}),makeQuery(id+"F2.opExtrude","SWEPT_FACE",FACE,{"disambiguationData":[OSD([subQ1,sQuery(id+"F0.wireOp",EDGE,"E9.1.3")])]})]}),makeQuery(id+"F3.opChamfer","SPLIT",FACE,{"disambiguationData":[OD(1.0)],"derivedFrom":makeQuery(id+"F2.boolean.opBoolean","MERGE",FACE,{"derivedFrom":[makeQuery(id+"F1.opExtrude","SWEPT_FACE",FACE,{"disambiguationData":[OSD([subQ0])]}),makeQuery(id+"F2.opExtrude","SWEPT_FACE",FACE,{"disambiguationData":[OSD([subQ0]),TDD([makeQuery(id+"F0.imprint","IMPRINT",EDGE,{"disambiguationData":[TD([[makeQuery(id+"F0.imprint","INTERSECT",VERTEX,{"derivedFrom":[subQ0,sQuery(id+"F0.wireOp",EDGE,"E6")]}),1.0]])],"derivedFrom":subQ0})])]}),makeQuery(id+"F2.opExtrude","SWEPT_FACE",FACE,{"disambiguationData":[OSD([subQ0]),TDD([makeQuery(id+"F0.imprint","IMPRINT",EDGE,{"disambiguationData":[TD([[makeQuery(id+"F0.imprint","INTERSECT",VERTEX,{"derivedFrom":[subQ0,subQ1]}),-1.0]])],"derivedFrom":subQ0})])]}),makeQuery(id+"F2.opExtrude","SWEPT_FACE",FACE,{"disambiguationData":[OSD([subQ0]),TDD([makeQuery(id+"F0.imprint","IMPRINT",EDGE,{"disambiguationData":[TD([[makeQuery(id+"F0.imprint","INTERSECT",VERTEX,{"derivedFrom":[subQ0,sQuery(id+"F0.wireOp",EDGE,"E9.2.0")]}),-1.0]])],"derivedFrom":subQ0})])]})]})})],"blendedInto":[makeQuery(id+"F3.opChamfer","SPLIT",FACE,{"disambiguationData":[OD(1.0)],"derivedFrom":makeQuery(id+"F2.boolean.opBoolean","MERGE",FACE,{"derivedFrom":[makeQuery(id+"F1.opExtrude","SWEPT_FACE",FACE,{"disambiguationData":[OSD([subQ0])]}),makeQuery(id+"F2.opExtrude","SWEPT_FACE",FACE,{"disambiguationData":[OSD([subQ0]),TDD([makeQuery(id+"F0.imprint","IMPRINT",EDGE,{"disambiguationData":[TD([[makeQuery(id+"F0.imprint","INTERSECT",VERTEX,{"derivedFrom":[subQ0,sQuery(id+"F0.wireOp",EDGE,"E6")]}),1.0]])],"derivedFrom":subQ0})])]}),makeQuery(id+"F2.opExtrude","SWEPT_FACE",FACE,{"disambiguationData":[OSD([subQ0]),TDD([makeQuery(id+"F0.imprint","IMPRINT",EDGE,{"disambiguationData":[TD([[makeQuery(id+"F0.imprint","INTERSECT",VERTEX,{"derivedFrom":[subQ0,subQ1]}),-1.0]])],"derivedFrom":subQ0})])]}),makeQuery(id+"F2.opExtrude","SWEPT_FACE",FACE,{"disambiguationData":[OSD([subQ0]),TDD([makeQuery(id+"F0.imprint","IMPRINT",EDGE,{"disambiguationData":[TD([[makeQuery(id+"F0.imprint","INTERSECT",VERTEX,{"derivedFrom":[subQ0,sQuery(id+"F0.wireOp",EDGE,"E9.2.0")]}),-1.0]])],"derivedFrom":subQ0})])]})]})})]});}
            var Q10;
            {var subQ0=sQuery(id+"F0.wireOp",EDGE,"E0");var subQ1=sQuery(id+"F0.wireOp",EDGE,"E9.1.1");Q10=makeQuery(id+"F9.opFillet","BLEND_EDGE",EDGE,{"blendedFrom":[makeQuery(id+"F2.boolean.opBoolean","INTERSECT",EDGE,{"derivedFrom":[makeQuery(id+"F1.opExtrude","CAP_FACE",FACE,{"disambiguationData":[OSD([subQ0,sQuery(id+"F0.wireOp",EDGE,"E3")])],"isStart":false}),makeQuery(id+"F2.opExtrude","SWEPT_FACE",FACE,{"disambiguationData":[OSD([subQ1,sQuery(id+"F0.wireOp",EDGE,"E9.1.2")])]})]}),makeQuery(id+"F3.opChamfer","SPLIT",FACE,{"disambiguationData":[OD(1.0)],"derivedFrom":makeQuery(id+"F2.boolean.opBoolean","MERGE",FACE,{"derivedFrom":[makeQuery(id+"F1.opExtrude","SWEPT_FACE",FACE,{"disambiguationData":[OSD([subQ0])]}),makeQuery(id+"F2.opExtrude","SWEPT_FACE",FACE,{"disambiguationData":[OSD([subQ0]),TDD([makeQuery(id+"F0.imprint","IMPRINT",EDGE,{"disambiguationData":[TD([[makeQuery(id+"F0.imprint","INTERSECT",VERTEX,{"derivedFrom":[subQ0,sQuery(id+"F0.wireOp",EDGE,"E6")]}),1.0]])],"derivedFrom":subQ0})])]}),makeQuery(id+"F2.opExtrude","SWEPT_FACE",FACE,{"disambiguationData":[OSD([subQ0]),TDD([makeQuery(id+"F0.imprint","IMPRINT",EDGE,{"disambiguationData":[TD([[makeQuery(id+"F0.imprint","INTERSECT",VERTEX,{"derivedFrom":[subQ0,sQuery(id+"F0.wireOp",EDGE,"E9.1.0")]}),-1.0]])],"derivedFrom":subQ0})])]}),makeQuery(id+"F2.opExtrude","SWEPT_FACE",FACE,{"disambiguationData":[OSD([subQ0]),TDD([makeQuery(id+"F0.imprint","IMPRINT",EDGE,{"disambiguationData":[TD([[makeQuery(id+"F0.imprint","INTERSECT",VERTEX,{"derivedFrom":[subQ0,sQuery(id+"F0.wireOp",EDGE,"E9.2.0")]}),-1.0]])],"derivedFrom":subQ0})])]})]})})],"blendedInto":[makeQuery(id+"F3.opChamfer","SPLIT",FACE,{"disambiguationData":[OD(1.0)],"derivedFrom":makeQuery(id+"F2.boolean.opBoolean","MERGE",FACE,{"derivedFrom":[makeQuery(id+"F1.opExtrude","SWEPT_FACE",FACE,{"disambiguationData":[OSD([subQ0])]}),makeQuery(id+"F2.opExtrude","SWEPT_FACE",FACE,{"disambiguationData":[OSD([subQ0]),TDD([makeQuery(id+"F0.imprint","IMPRINT",EDGE,{"disambiguationData":[TD([[makeQuery(id+"F0.imprint","INTERSECT",VERTEX,{"derivedFrom":[subQ0,sQuery(id+"F0.wireOp",EDGE,"E6")]}),1.0]])],"derivedFrom":subQ0})])]}),makeQuery(id+"F2.opExtrude","SWEPT_FACE",FACE,{"disambiguationData":[OSD([subQ0]),TDD([makeQuery(id+"F0.imprint","IMPRINT",EDGE,{"disambiguationData":[TD([[makeQuery(id+"F0.imprint","INTERSECT",VERTEX,{"derivedFrom":[subQ0,sQuery(id+"F0.wireOp",EDGE,"E9.1.0")]}),-1.0]])],"derivedFrom":subQ0})])]}),makeQuery(id+"F2.opExtrude","SWEPT_FACE",FACE,{"disambiguationData":[OSD([subQ0]),TDD([makeQuery(id+"F0.imprint","IMPRINT",EDGE,{"disambiguationData":[TD([[makeQuery(id+"F0.imprint","INTERSECT",VERTEX,{"derivedFrom":[subQ0,sQuery(id+"F0.wireOp",EDGE,"E9.2.0")]}),-1.0]])],"derivedFrom":subQ0})])]})]})})]});}
            var Q11;
            {var subQ0=sQuery(id+"F0.wireOp",EDGE,"E9.2.0");var subQ1=sQuery(id+"F0.wireOp",EDGE,"E0");Q11=makeQuery(id+"F9.opFillet","BLEND_EDGE",EDGE,{"blendedFrom":[makeQuery(id+"F2.boolean.opBoolean","INTERSECT",EDGE,{"derivedFrom":[makeQuery(id+"F1.opExtrude","CAP_FACE",FACE,{"disambiguationData":[OSD([subQ1,sQuery(id+"F0.wireOp",EDGE,"E3")])],"isStart":false}),makeQuery(id+"F2.opExtrude","SWEPT_FACE",FACE,{"disambiguationData":[OSD([subQ0,sQuery(id+"F0.wireOp",EDGE,"E9.2.3")])]})]}),makeQuery(id+"F3.opChamfer","SPLIT",FACE,{"disambiguationData":[OD(2.0)],"derivedFrom":makeQuery(id+"F2.boolean.opBoolean","MERGE",FACE,{"derivedFrom":[makeQuery(id+"F1.opExtrude","SWEPT_FACE",FACE,{"disambiguationData":[OSD([subQ1])]}),makeQuery(id+"F2.opExtrude","SWEPT_FACE",FACE,{"disambiguationData":[OSD([subQ1]),TDD([makeQuery(id+"F0.imprint","IMPRINT",EDGE,{"disambiguationData":[TD([[makeQuery(id+"F0.imprint","INTERSECT",VERTEX,{"derivedFrom":[subQ1,sQuery(id+"F0.wireOp",EDGE,"E6")]}),1.0]])],"derivedFrom":subQ1})])]}),makeQuery(id+"F2.opExtrude","SWEPT_FACE",FACE,{"disambiguationData":[OSD([subQ1]),TDD([makeQuery(id+"F0.imprint","IMPRINT",EDGE,{"disambiguationData":[TD([[makeQuery(id+"F0.imprint","INTERSECT",VERTEX,{"derivedFrom":[subQ1,sQuery(id+"F0.wireOp",EDGE,"E9.1.0")]}),-1.0]])],"derivedFrom":subQ1})])]}),makeQuery(id+"F2.opExtrude","SWEPT_FACE",FACE,{"disambiguationData":[OSD([subQ1]),TDD([makeQuery(id+"F0.imprint","IMPRINT",EDGE,{"disambiguationData":[TD([[makeQuery(id+"F0.imprint","INTERSECT",VERTEX,{"derivedFrom":[subQ1,subQ0]}),-1.0]])],"derivedFrom":subQ1})])]})]})})],"blendedInto":[makeQuery(id+"F3.opChamfer","SPLIT",FACE,{"disambiguationData":[OD(2.0)],"derivedFrom":makeQuery(id+"F2.boolean.opBoolean","MERGE",FACE,{"derivedFrom":[makeQuery(id+"F1.opExtrude","SWEPT_FACE",FACE,{"disambiguationData":[OSD([subQ1])]}),makeQuery(id+"F2.opExtrude","SWEPT_FACE",FACE,{"disambiguationData":[OSD([subQ1]),TDD([makeQuery(id+"F0.imprint","IMPRINT",EDGE,{"disambiguationData":[TD([[makeQuery(id+"F0.imprint","INTERSECT",VERTEX,{"derivedFrom":[subQ1,sQuery(id+"F0.wireOp",EDGE,"E6")]}),1.0]])],"derivedFrom":subQ1})])]}),makeQuery(id+"F2.opExtrude","SWEPT_FACE",FACE,{"disambiguationData":[OSD([subQ1]),TDD([makeQuery(id+"F0.imprint","IMPRINT",EDGE,{"disambiguationData":[TD([[makeQuery(id+"F0.imprint","INTERSECT",VERTEX,{"derivedFrom":[subQ1,sQuery(id+"F0.wireOp",EDGE,"E9.1.0")]}),-1.0]])],"derivedFrom":subQ1})])]}),makeQuery(id+"F2.opExtrude","SWEPT_FACE",FACE,{"disambiguationData":[OSD([subQ1]),TDD([makeQuery(id+"F0.imprint","IMPRINT",EDGE,{"disambiguationData":[TD([[makeQuery(id+"F0.imprint","INTERSECT",VERTEX,{"derivedFrom":[subQ1,subQ0]}),-1.0]])],"derivedFrom":subQ1})])]})]})})]});}
            var Q12;
            {var subQ0=sQuery(id+"F0.wireOp",EDGE,"E0");var subQ1=makeQuery(id+"F0.imprint","IMPRINT",EDGE,{"disambiguationData":[TD([[makeQuery(id+"F0.imprint","INTERSECT",VERTEX,{"derivedFrom":[subQ0,sQuery(id+"F0.wireOp",EDGE,"E9.2.0")]}),-1.0]])],"derivedFrom":subQ0});Q12=makeQuery(id+"F6.opChamfer","BLEND_EDGE",EDGE,{"blendedFrom":[makeQuery(id+"F2.opExtrude","CAP_EDGE",EDGE,{"disambiguationData":[OSD([subQ0]),TDD([subQ1])],"isStart":false}),makeQuery(id+"F3.opChamfer","SPLIT",FACE,{"disambiguationData":[OD(2.0)],"derivedFrom":makeQuery(id+"F2.boolean.opBoolean","MERGE",FACE,{"derivedFrom":[makeQuery(id+"F1.opExtrude","SWEPT_FACE",FACE,{"disambiguationData":[OSD([subQ0])]}),makeQuery(id+"F2.opExtrude","SWEPT_FACE",FACE,{"disambiguationData":[OSD([subQ0]),TDD([makeQuery(id+"F0.imprint","IMPRINT",EDGE,{"disambiguationData":[TD([[makeQuery(id+"F0.imprint","INTERSECT",VERTEX,{"derivedFrom":[subQ0,sQuery(id+"F0.wireOp",EDGE,"E6")]}),1.0]])],"derivedFrom":subQ0})])]}),makeQuery(id+"F2.opExtrude","SWEPT_FACE",FACE,{"disambiguationData":[OSD([subQ0]),TDD([makeQuery(id+"F0.imprint","IMPRINT",EDGE,{"disambiguationData":[TD([[makeQuery(id+"F0.imprint","INTERSECT",VERTEX,{"derivedFrom":[subQ0,sQuery(id+"F0.wireOp",EDGE,"E9.1.0")]}),-1.0]])],"derivedFrom":subQ0})])]}),makeQuery(id+"F2.opExtrude","SWEPT_FACE",FACE,{"disambiguationData":[OSD([subQ0]),TDD([subQ1])]})]})})],"blendedInto":[makeQuery(id+"F3.opChamfer","SPLIT",FACE,{"disambiguationData":[OD(2.0)],"derivedFrom":makeQuery(id+"F2.boolean.opBoolean","MERGE",FACE,{"derivedFrom":[makeQuery(id+"F1.opExtrude","SWEPT_FACE",FACE,{"disambiguationData":[OSD([subQ0])]}),makeQuery(id+"F2.opExtrude","SWEPT_FACE",FACE,{"disambiguationData":[OSD([subQ0]),TDD([makeQuery(id+"F0.imprint","IMPRINT",EDGE,{"disambiguationData":[TD([[makeQuery(id+"F0.imprint","INTERSECT",VERTEX,{"derivedFrom":[subQ0,sQuery(id+"F0.wireOp",EDGE,"E6")]}),1.0]])],"derivedFrom":subQ0})])]}),makeQuery(id+"F2.opExtrude","SWEPT_FACE",FACE,{"disambiguationData":[OSD([subQ0]),TDD([makeQuery(id+"F0.imprint","IMPRINT",EDGE,{"disambiguationData":[TD([[makeQuery(id+"F0.imprint","INTERSECT",VERTEX,{"derivedFrom":[subQ0,sQuery(id+"F0.wireOp",EDGE,"E9.1.0")]}),-1.0]])],"derivedFrom":subQ0})])]}),makeQuery(id+"F2.opExtrude","SWEPT_FACE",FACE,{"disambiguationData":[OSD([subQ0]),TDD([subQ1])]})]})})]});}
            var Q13;
            {var subQ0=sQuery(id+"F0.wireOp",EDGE,"E0");var subQ1=sQuery(id+"F0.wireOp",EDGE,"E9.2.1");Q13=makeQuery(id+"F9.opFillet","BLEND_EDGE",EDGE,{"blendedFrom":[makeQuery(id+"F2.boolean.opBoolean","INTERSECT",EDGE,{"derivedFrom":[makeQuery(id+"F1.opExtrude","CAP_FACE",FACE,{"disambiguationData":[OSD([subQ0,sQuery(id+"F0.wireOp",EDGE,"E3")])],"isStart":false}),makeQuery(id+"F2.opExtrude","SWEPT_FACE",FACE,{"disambiguationData":[OSD([subQ1,sQuery(id+"F0.wireOp",EDGE,"E9.2.2")])]})]}),makeQuery(id+"F3.opChamfer","SPLIT",FACE,{"disambiguationData":[OD(2.0)],"derivedFrom":makeQuery(id+"F2.boolean.opBoolean","MERGE",FACE,{"derivedFrom":[makeQuery(id+"F1.opExtrude","SWEPT_FACE",FACE,{"disambiguationData":[OSD([subQ0])]}),makeQuery(id+"F2.opExtrude","SWEPT_FACE",FACE,{"disambiguationData":[OSD([subQ0]),TDD([makeQuery(id+"F0.imprint","IMPRINT",EDGE,{"disambiguationData":[TD([[makeQuery(id+"F0.imprint","INTERSECT",VERTEX,{"derivedFrom":[subQ0,sQuery(id+"F0.wireOp",EDGE,"E6")]}),1.0]])],"derivedFrom":subQ0})])]}),makeQuery(id+"F2.opExtrude","SWEPT_FACE",FACE,{"disambiguationData":[OSD([subQ0]),TDD([makeQuery(id+"F0.imprint","IMPRINT",EDGE,{"disambiguationData":[TD([[makeQuery(id+"F0.imprint","INTERSECT",VERTEX,{"derivedFrom":[subQ0,sQuery(id+"F0.wireOp",EDGE,"E9.1.0")]}),-1.0]])],"derivedFrom":subQ0})])]}),makeQuery(id+"F2.opExtrude","SWEPT_FACE",FACE,{"disambiguationData":[OSD([subQ0]),TDD([makeQuery(id+"F0.imprint","IMPRINT",EDGE,{"disambiguationData":[TD([[makeQuery(id+"F0.imprint","INTERSECT",VERTEX,{"derivedFrom":[subQ0,sQuery(id+"F0.wireOp",EDGE,"E9.2.0")]}),-1.0]])],"derivedFrom":subQ0})])]})]})})],"blendedInto":[makeQuery(id+"F3.opChamfer","SPLIT",FACE,{"disambiguationData":[OD(2.0)],"derivedFrom":makeQuery(id+"F2.boolean.opBoolean","MERGE",FACE,{"derivedFrom":[makeQuery(id+"F1.opExtrude","SWEPT_FACE",FACE,{"disambiguationData":[OSD([subQ0])]}),makeQuery(id+"F2.opExtrude","SWEPT_FACE",FACE,{"disambiguationData":[OSD([subQ0]),TDD([makeQuery(id+"F0.imprint","IMPRINT",EDGE,{"disambiguationData":[TD([[makeQuery(id+"F0.imprint","INTERSECT",VERTEX,{"derivedFrom":[subQ0,sQuery(id+"F0.wireOp",EDGE,"E6")]}),1.0]])],"derivedFrom":subQ0})])]}),makeQuery(id+"F2.opExtrude","SWEPT_FACE",FACE,{"disambiguationData":[OSD([subQ0]),TDD([makeQuery(id+"F0.imprint","IMPRINT",EDGE,{"disambiguationData":[TD([[makeQuery(id+"F0.imprint","INTERSECT",VERTEX,{"derivedFrom":[subQ0,sQuery(id+"F0.wireOp",EDGE,"E9.1.0")]}),-1.0]])],"derivedFrom":subQ0})])]}),makeQuery(id+"F2.opExtrude","SWEPT_FACE",FACE,{"disambiguationData":[OSD([subQ0]),TDD([makeQuery(id+"F0.imprint","IMPRINT",EDGE,{"disambiguationData":[TD([[makeQuery(id+"F0.imprint","INTERSECT",VERTEX,{"derivedFrom":[subQ0,sQuery(id+"F0.wireOp",EDGE,"E9.2.0")]}),-1.0]])],"derivedFrom":subQ0})])]})]})})]});}
            var Q14;
            {var subQ0=sQuery(id+"F4.wireOp",EDGE,"E11");Q14=makeQuery(id+"F5.boolean.opBoolean","SPLIT",EDGE,{"disambiguationData":[TD([makeQuery(id+"F2.opExtrude","SWEPT_FACE",FACE,{"disambiguationData":[OSD([sQuery(id+"F0.wireOp",EDGE,"E9.1.1"),sQuery(id+"F0.wireOp",EDGE,"E9.1.2")])]})])],"derivedFrom":makeQuery(id+"F5.opExtrude","CAP_EDGE",EDGE,{"disambiguationData":[OSD([subQ0])],"isStart":true})});}
            var Q15;
            {var subQ0=sQuery(id+"F0.wireOp",EDGE,"E0");var subQ1=sQuery(id+"F0.wireOp",EDGE,"E9.1.1");var subQ2=sQuery(id+"F0.wireOp",EDGE,"E3");var subQ5=makeQuery(id+"F2.opExtrude","SWEPT_FACE",FACE,{"disambiguationData":[OSD([subQ1,sQuery(id+"F0.wireOp",EDGE,"E9.1.2")])]});var subQ7=makeQuery(id+"F1.opExtrude","CAP_FACE",FACE,{"disambiguationData":[OSD([subQ0,subQ2])],"isStart":false});Q15=makeQuery(id+"F3.opChamfer","BLEND_EDGE",EDGE,{"blendedFrom":[makeQuery(id+"F2.boolean.opBoolean","SPLIT",EDGE,{"disambiguationData":[TD([subQ5])],"derivedFrom":makeQuery(id+"F1.opExtrude","CAP_EDGE",EDGE,{"disambiguationData":[OSD([subQ2])],"isStart":false})}),makeQuery(id+"F2.boolean.opBoolean","SPLIT",FACE,{"disambiguationData":[TD([subQ5])],"derivedFrom":subQ7})],"blendedInto":[makeQuery(id+"F2.boolean.opBoolean","SPLIT",FACE,{"disambiguationData":[TD([subQ5])],"derivedFrom":subQ7})]});}
            var Q16;
            {var subQ0=sQuery(id+"F0.wireOp",EDGE,"E0");var subQ3=sQuery(id+"F0.wireOp",EDGE,"E7");var subQ4=sQuery(id+"F0.wireOp",EDGE,"E3");var subQ6=makeQuery(id+"F2.opExtrude","SWEPT_FACE",FACE,{"disambiguationData":[OSD([sQuery(id+"F0.wireOp",EDGE,"E5"),subQ3])]});var subQ7=makeQuery(id+"F1.opExtrude","CAP_FACE",FACE,{"disambiguationData":[OSD([subQ0,subQ4])],"isStart":false});Q16=makeQuery(id+"F3.opChamfer","BLEND_EDGE",EDGE,{"blendedFrom":[makeQuery(id+"F2.boolean.opBoolean","SPLIT",EDGE,{"disambiguationData":[TD([subQ6])],"derivedFrom":makeQuery(id+"F1.opExtrude","CAP_EDGE",EDGE,{"disambiguationData":[OSD([subQ4])],"isStart":false})}),makeQuery(id+"F2.boolean.opBoolean","SPLIT",FACE,{"disambiguationData":[TD([subQ6])],"derivedFrom":subQ7})],"blendedInto":[makeQuery(id+"F2.boolean.opBoolean","SPLIT",FACE,{"disambiguationData":[TD([subQ6])],"derivedFrom":subQ7})]});}
            var Q17;
            {var subQ1=sQuery(id+"F0.wireOp",EDGE,"E0");var subQ2=sQuery(id+"F0.wireOp",EDGE,"E6");var subQ4=sQuery(id+"F0.wireOp",EDGE,"E3");var subQ6=makeQuery(id+"F2.opExtrude","SWEPT_FACE",FACE,{"disambiguationData":[OSD([sQuery(id+"F0.wireOp",EDGE,"E4"),subQ2])]});var subQ7=makeQuery(id+"F1.opExtrude","CAP_FACE",FACE,{"disambiguationData":[OSD([subQ1,subQ4])],"isStart":false});Q17=makeQuery(id+"F3.opChamfer","BLEND_EDGE",EDGE,{"blendedFrom":[makeQuery(id+"F2.boolean.opBoolean","SPLIT",EDGE,{"disambiguationData":[TD([subQ6])],"derivedFrom":makeQuery(id+"F1.opExtrude","CAP_EDGE",EDGE,{"disambiguationData":[OSD([subQ4])],"isStart":false})}),makeQuery(id+"F2.boolean.opBoolean","SPLIT",FACE,{"disambiguationData":[TD([subQ6])],"derivedFrom":subQ7})],"blendedInto":[makeQuery(id+"F2.boolean.opBoolean","SPLIT",FACE,{"disambiguationData":[TD([subQ6])],"derivedFrom":subQ7})]});}
            var Q18;
            {var subQ0=sQuery(id+"F4.wireOp",EDGE,"E11");Q18=makeQuery(id+"F5.boolean.opBoolean","SPLIT",EDGE,{"disambiguationData":[TD([makeQuery(id+"F2.opExtrude","SWEPT_FACE",FACE,{"disambiguationData":[OSD([sQuery(id+"F0.wireOp",EDGE,"E5"),sQuery(id+"F0.wireOp",EDGE,"E7")])]})])],"derivedFrom":makeQuery(id+"F5.opExtrude","CAP_EDGE",EDGE,{"disambiguationData":[OSD([subQ0])],"isStart":true})});}
            var Q19;
            {var subQ0=sQuery(id+"F4.wireOp",EDGE,"E11");Q19=makeQuery(id+"F5.boolean.opBoolean","SPLIT",EDGE,{"disambiguationData":[TD([makeQuery(id+"F2.opExtrude","SWEPT_FACE",FACE,{"disambiguationData":[OSD([sQuery(id+"F0.wireOp",EDGE,"E4"),sQuery(id+"F0.wireOp",EDGE,"E6")])]})])],"derivedFrom":makeQuery(id+"F5.opExtrude","CAP_EDGE",EDGE,{"disambiguationData":[OSD([subQ0])],"isStart":true})});}
            fillet(context, id + "F8", {"entities" : qUnion([Q0, Q1, Q2, Q3, Q4, Q5, Q6, Q7, Q8, Q9, Q10, Q11, Q12, Q13, Q14, Q15, Q16, Q17, Q18, Q19]), "radius" : .5 * mm, "tangentPropagation" : true, "defaultsChanged" : false, "vertexSettings" : [], "allowEdgeOverflow" : false});
        }
        {
            var Q0;
            Q0=makeQuery(id+"F2.opExtrude","SWEPT_EDGE",EDGE,{"disambiguationData":[OSD([sQuery(id+"F0.wireOp",EDGE,"E2"),sQuery(id+"F0.wireOp",EDGE,"E9.1.2")])]});
            var Q1;
            Q1=makeQuery(id+"F2.opExtrude","SWEPT_EDGE",EDGE,{"disambiguationData":[OSD([sQuery(id+"F0.wireOp",EDGE,"E2"),sQuery(id+"F0.wireOp",EDGE,"E9.2.3")])]});
            var Q2;
            Q2=makeQuery(id+"F2.opExtrude","SWEPT_EDGE",EDGE,{"disambiguationData":[OSD([sQuery(id+"F0.wireOp",EDGE,"E2"),sQuery(id+"F0.wireOp",EDGE,"E9.1.3")])]});
            var Q3;
            Q3=makeQuery(id+"F2.opExtrude","SWEPT_EDGE",EDGE,{"disambiguationData":[OSD([sQuery(id+"F0.wireOp",EDGE,"E2"),sQuery(id+"F0.wireOp",EDGE,"E4")])]});
            var Q4;
            Q4=makeQuery(id+"F2.opExtrude","SWEPT_EDGE",EDGE,{"disambiguationData":[OSD([sQuery(id+"F0.wireOp",EDGE,"E2"),sQuery(id+"F0.wireOp",EDGE,"E9.2.2")])]});
            var Q5;
            Q5=makeQuery(id+"F2.opExtrude","SWEPT_EDGE",EDGE,{"disambiguationData":[OSD([sQuery(id+"F0.wireOp",EDGE,"E2"),sQuery(id+"F0.wireOp",EDGE,"E5")])]});
            fillet(context, id + "F9", {"entities" : qUnion([Q0, Q1, Q2, Q3, Q4, Q5]), "radius" : 2 * mm, "tangentPropagation" : true, "defaultsChanged" : false, "vertexSettings" : [], "allowEdgeOverflow" : false});
        }
        {
            var Q0;
            {var subQ0=sQuery(id+"F0.wireOp",EDGE,"7a49S09U-4TKs-Mau8-UFGr-jYDSAMmVkobc");var subQ1=sQuery(id+"F0.wireOp",EDGE,"E0");var subQ2=makeQuery(id+"F0.imprint","INTERSECT",VERTEX,{"derivedFrom":[subQ1,subQ0]});Q0=makeQuery(id+"F0.imprint","IMPRINT",FACE,{"disambiguationData":[TD([[makeQuery(id+"F0.imprint","IMPRINT",EDGE,{"disambiguationData":[TD([[subQ2,1.0]])],"derivedFrom":subQ1}),1.0]])]});}
            var Q1;
            {var subQ0=sQuery(id+"F0.wireOp",EDGE,"7a49S09U-4TKs-Mau8-UFGr-jYDSAMmVkobc");var subQ1=sQuery(id+"F0.wireOp",EDGE,"E0");var subQ2=makeQuery(id+"F0.imprint","INTERSECT",VERTEX,{"derivedFrom":[subQ1,subQ0]});Q1=makeQuery(id+"F0.imprint","IMPRINT",FACE,{"disambiguationData":[TD([[makeQuery(id+"F0.imprint","IMPRINT",EDGE,{"disambiguationData":[TD([[subQ2,-1.0]])],"derivedFrom":subQ1}),1.0]])]});}
            var Q2;
            {var subQ0=sQuery(id+"F0.wireOp",EDGE,"6sBZeKKk-kEEp-gHMs-JJ9J-U2pvovovTZg0");var subQ1=sQuery(id+"F0.wireOp",EDGE,"E0");var subQ2=makeQuery(id+"F0.imprint","INTERSECT",VERTEX,{"derivedFrom":[subQ1,subQ0]});Q2=makeQuery(id+"F0.imprint","IMPRINT",FACE,{"disambiguationData":[TD([[makeQuery(id+"F0.imprint","IMPRINT",EDGE,{"disambiguationData":[TD([[subQ2,1.0]])],"derivedFrom":subQ1}),1.0]])]});}
            var Q3;
            {var subQ0=sQuery(id+"F0.wireOp",EDGE,"E6");var subQ1=sQuery(id+"F0.wireOp",EDGE,"E0");var subQ2=makeQuery(id+"F0.imprint","INTERSECT",VERTEX,{"derivedFrom":[subQ1,subQ0]});Q3=makeQuery(id+"F0.imprint","IMPRINT",FACE,{"disambiguationData":[TD([[makeQuery(id+"F0.imprint","IMPRINT",EDGE,{"disambiguationData":[TD([[subQ2,-1.0]])],"derivedFrom":subQ1}),1.0]])]});}
            var Q4;
            {var subQ0=sQuery(id+"F0.wireOp",EDGE,"64FUqdOZ-ZsVY-jkXw-3n9p-KAZBQBVsTFE5");var subQ1=sQuery(id+"F0.wireOp",EDGE,"E0");var subQ2=makeQuery(id+"F0.imprint","INTERSECT",VERTEX,{"derivedFrom":[subQ1,subQ0]});Q4=makeQuery(id+"F0.imprint","IMPRINT",FACE,{"disambiguationData":[TD([[makeQuery(id+"F0.imprint","IMPRINT",EDGE,{"disambiguationData":[TD([[subQ2,-1.0]])],"derivedFrom":subQ1}),1.0]])]});}
            var Q5;
            {var subQ0=sQuery(id+"F0.wireOp",EDGE,"E6");var subQ1=sQuery(id+"F0.wireOp",EDGE,"E0");var subQ2=makeQuery(id+"F0.imprint","INTERSECT",VERTEX,{"derivedFrom":[subQ1,subQ0]});Q5=makeQuery(id+"F0.imprint","IMPRINT",FACE,{"disambiguationData":[TD([[makeQuery(id+"F0.imprint","IMPRINT",EDGE,{"disambiguationData":[TD([[subQ2,1.0]])],"derivedFrom":subQ1}),1.0]])]});}
            var Q6;
            {var subQ0=sQuery(id+"F0.wireOp",EDGE,"E7");var subQ1=sQuery(id+"F0.wireOp",EDGE,"E0");var subQ2=makeQuery(id+"F0.imprint","INTERSECT",VERTEX,{"derivedFrom":[subQ1,subQ0]});Q6=makeQuery(id+"F0.imprint","IMPRINT",FACE,{"disambiguationData":[TD([[makeQuery(id+"F0.imprint","IMPRINT",EDGE,{"disambiguationData":[TD([[subQ2,1.0]])],"derivedFrom":subQ1}),1.0]])]});}
            var Q7;
            {var subQ0=sQuery(id+"F0.wireOp",EDGE,"kpPb6oPH-wYUV-R5u9-Nvo8-y8tA6iOcowlW");var subQ1=sQuery(id+"F0.wireOp",EDGE,"E0");var subQ2=makeQuery(id+"F0.imprint","INTERSECT",VERTEX,{"derivedFrom":[subQ1,subQ0]});Q7=makeQuery(id+"F0.imprint","IMPRINT",FACE,{"disambiguationData":[TD([[makeQuery(id+"F0.imprint","IMPRINT",EDGE,{"disambiguationData":[TD([[subQ2,1.0]])],"derivedFrom":subQ1}),1.0]])]});}
            extrude(context, id + "F10", {"entities" : qUnion([Q0, Q1, Q2, Q3, Q4, Q5, Q6, Q7]), "operationType" : NewBodyOperationType.REMOVE, "endBound" : BoundingType.THROUGH_ALL, "depth" : 25 * mm, "offsetDistance" : 25 * mm});
        }
        {
            var Q0;
            {var subQ0=sQuery(id+"F0.wireOp",EDGE,"E3");Q0=makeQuery(id+"F5.boolean.opBoolean","INTERSECT",EDGE,{"derivedFrom":[makeQuery(id+"F3.opChamfer","BLEND_FACE",FACE,{"disambiguationData":[OSD([subQ0]),TDD([makeQuery(id+"F2.boolean.opBoolean","SPLIT",EDGE,{"disambiguationData":[TD([makeQuery(id+"F2.opExtrude","SWEPT_FACE",FACE,{"disambiguationData":[OSD([sQuery(id+"F0.wireOp",EDGE,"E4"),sQuery(id+"F0.wireOp",EDGE,"E6")])]})])],"derivedFrom":makeQuery(id+"F1.opExtrude","CAP_EDGE",EDGE,{"disambiguationData":[OSD([subQ0])],"isStart":false})})])]}),makeQuery(id+"F5.opExtrude","CAP_FACE",FACE,{"disambiguationData":[OSD([sQuery(id+"F4.wireOp",EDGE,"E10"),sQuery(id+"F4.wireOp",EDGE,"E11")])],"isStart":true})]});}
            var Q1;
            {var subQ0=sQuery(id+"F0.wireOp",EDGE,"E3");Q1=makeQuery(id+"F5.boolean.opBoolean","INTERSECT",EDGE,{"derivedFrom":[makeQuery(id+"F3.opChamfer","BLEND_FACE",FACE,{"disambiguationData":[OSD([subQ0]),TDD([makeQuery(id+"F2.boolean.opBoolean","SPLIT",EDGE,{"disambiguationData":[TD([makeQuery(id+"F2.opExtrude","SWEPT_FACE",FACE,{"disambiguationData":[OSD([sQuery(id+"F0.wireOp",EDGE,"E9.1.1"),sQuery(id+"F0.wireOp",EDGE,"E9.1.2")])]})])],"derivedFrom":makeQuery(id+"F1.opExtrude","CAP_EDGE",EDGE,{"disambiguationData":[OSD([subQ0])],"isStart":false})})])]}),makeQuery(id+"F5.opExtrude","CAP_FACE",FACE,{"disambiguationData":[OSD([sQuery(id+"F4.wireOp",EDGE,"E10"),sQuery(id+"F4.wireOp",EDGE,"E11")])],"isStart":true})]});}
            var Q2;
            {var subQ0=sQuery(id+"F0.wireOp",EDGE,"E3");Q2=makeQuery(id+"F5.boolean.opBoolean","INTERSECT",EDGE,{"derivedFrom":[makeQuery(id+"F3.opChamfer","BLEND_FACE",FACE,{"disambiguationData":[OSD([subQ0]),TDD([makeQuery(id+"F2.boolean.opBoolean","SPLIT",EDGE,{"disambiguationData":[TD([makeQuery(id+"F2.opExtrude","SWEPT_FACE",FACE,{"disambiguationData":[OSD([sQuery(id+"F0.wireOp",EDGE,"E5"),sQuery(id+"F0.wireOp",EDGE,"E7")])]})])],"derivedFrom":makeQuery(id+"F1.opExtrude","CAP_EDGE",EDGE,{"disambiguationData":[OSD([subQ0])],"isStart":false})})])]}),makeQuery(id+"F5.opExtrude","CAP_FACE",FACE,{"disambiguationData":[OSD([sQuery(id+"F4.wireOp",EDGE,"E10"),sQuery(id+"F4.wireOp",EDGE,"E11")])],"isStart":true})]});}
            fillet(context, id + "F11", {"entities" : qUnion([Q0, Q1, Q2]), "tangentPropagation" : true, "radius" : 35 * mm, "defaultsChanged" : false, "vertexSettings" : [], "allowEdgeOverflow" : false});
        }
        {
            var Q0;
            Q0=makeQuery(id+"F5.opExtrude","CAP_EDGE",EDGE,{"disambiguationData":[OSD([sQuery(id+"F4.wireOp",EDGE,"E10")])],"isStart":false});
            chamfer(context, id + "F12", {"entities" : qUnion([Q0]), "width" : 0.5 * mm, "tangentPropagation" : true});
        }
    });
